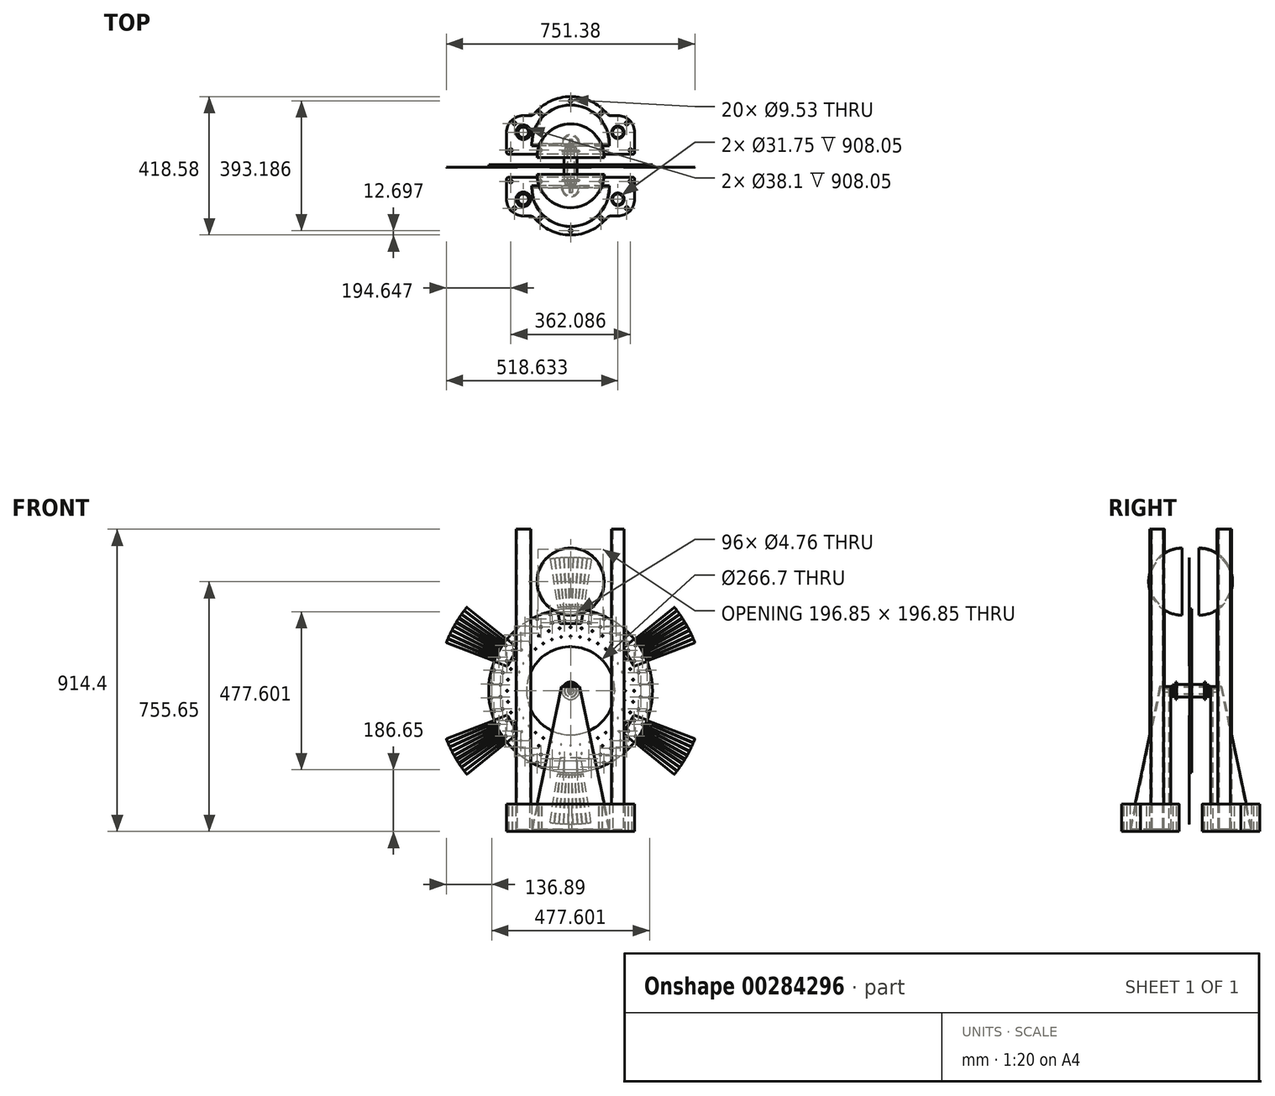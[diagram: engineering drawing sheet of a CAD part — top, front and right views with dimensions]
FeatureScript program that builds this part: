
annotation { "Feature Type Name" : "Feature", "Feature Type Description" : "" }
export const myFeature = defineFeature(function(context is Context, id is Id, definition is map)
    precondition{}
    {
        {
            var Q0;
            Q0=qCreatedBy(makeId("Front.planeOp"),FACE);
            var sketch = newSketch(context, id + "F0", { "sketchPlane" : qUnion([Q0])});
            skLineSegment(sketch, "E0", {"start": v(0, 0) * mm, "end": v(457.2, 0) * mm, "construction": true});
            skCircle(sketch, "E1", {"center": v(0, 0) * mm, "radius": 247.65 * mm});
            skCircle(sketch, "E2", {"center": v(0, 0) * mm, "radius": 133.35 * mm});
            skCircle(sketch, "E3", {"center": v(192.18, 0) * mm, "radius": 2 * mm});
            skCircle(sketch, "E4.1.0", {"center": v(189.26, 33.37) * mm, "radius": 2 * mm});
            skCircle(sketch, "E4.2.0", {"center": v(180.59, 65.73) * mm, "radius": 2 * mm});
            skCircle(sketch, "E4.3.0", {"center": v(166.43, 96.09) * mm, "radius": 2 * mm});
            skCircle(sketch, "E4.4.0", {"center": v(147.22, 123.53) * mm, "radius": 2 * mm});
            skCircle(sketch, "E4.5.0", {"center": v(123.53, 147.22) * mm, "radius": 2 * mm});
            skCircle(sketch, "E4.6.0", {"center": v(96.09, 166.43) * mm, "radius": 2 * mm});
            skCircle(sketch, "E4.7.0", {"center": v(65.73, 180.59) * mm, "radius": 2 * mm});
            skCircle(sketch, "E4.8.0", {"center": v(33.37, 189.26) * mm, "radius": 2 * mm});
            skCircle(sketch, "E4.9.0", {"center": v(0, 192.18) * mm, "radius": 2 * mm});
            skCircle(sketch, "E4.10.0", {"center": v(-33.37, 189.26) * mm, "radius": 2 * mm});
            skCircle(sketch, "E4.11.0", {"center": v(-65.73, 180.59) * mm, "radius": 2 * mm});
            skCircle(sketch, "E4.12.0", {"center": v(-96.09, 166.43) * mm, "radius": 2 * mm});
            skCircle(sketch, "E4.13.0", {"center": v(-123.53, 147.22) * mm, "radius": 2 * mm});
            skCircle(sketch, "E4.14.0", {"center": v(-147.22, 123.53) * mm, "radius": 2 * mm});
            skCircle(sketch, "E4.15.0", {"center": v(-166.43, 96.09) * mm, "radius": 2 * mm});
            skCircle(sketch, "E4.16.0", {"center": v(-180.59, 65.73) * mm, "radius": 2 * mm});
            skCircle(sketch, "E4.17.0", {"center": v(-189.26, 33.37) * mm, "radius": 2 * mm});
            skCircle(sketch, "E4.18.0", {"center": v(-192.18, 0) * mm, "radius": 2 * mm});
            skCircle(sketch, "E4.19.0", {"center": v(-189.26, -33.37) * mm, "radius": 2 * mm});
            skCircle(sketch, "E4.20.0", {"center": v(-180.59, -65.73) * mm, "radius": 2 * mm});
            skCircle(sketch, "E4.21.0", {"center": v(-166.43, -96.09) * mm, "radius": 2 * mm});
            skCircle(sketch, "E4.22.0", {"center": v(-147.22, -123.53) * mm, "radius": 2 * mm});
            skCircle(sketch, "E4.23.0", {"center": v(-123.53, -147.22) * mm, "radius": 2 * mm});
            skCircle(sketch, "E4.24.0", {"center": v(-96.09, -166.43) * mm, "radius": 2 * mm});
            skCircle(sketch, "E4.25.0", {"center": v(-65.73, -180.59) * mm, "radius": 2 * mm});
            skCircle(sketch, "E4.26.0", {"center": v(-33.37, -189.26) * mm, "radius": 2 * mm});
            skCircle(sketch, "E4.27.0", {"center": v(0, -192.18) * mm, "radius": 2 * mm});
            skCircle(sketch, "E4.28.0", {"center": v(33.37, -189.26) * mm, "radius": 2 * mm});
            skCircle(sketch, "E4.29.0", {"center": v(65.73, -180.59) * mm, "radius": 2 * mm});
            skCircle(sketch, "E4.30.0", {"center": v(96.09, -166.43) * mm, "radius": 2 * mm});
            skCircle(sketch, "E4.31.0", {"center": v(123.53, -147.22) * mm, "radius": 2 * mm});
            skCircle(sketch, "E4.32.0", {"center": v(147.22, -123.53) * mm, "radius": 2 * mm});
            skCircle(sketch, "E4.33.0", {"center": v(166.43, -96.09) * mm, "radius": 2 * mm});
            skCircle(sketch, "E4.34.0", {"center": v(180.59, -65.73) * mm, "radius": 2 * mm});
            skCircle(sketch, "E4.35.0", {"center": v(189.26, -33.37) * mm, "radius": 2 * mm});
            skCircle(sketch, "E5", {"center": v(165.1, 0) * mm, "radius": 1.59 * mm});
            skLineSegment(sketch, "E6", {"start": v(0, 0) * mm, "end": v(246.7, 21.58) * mm, "construction": true});
            skCircle(sketch, "E7", {"center": v(238.8, 20.9) * mm, "radius": 2.38 * mm});
            skCircle(sketch, "E8", {"center": v(211.92, 18.54) * mm, "radius": 2.38 * mm});
            skCircle(sketch, "E9.1.0", {"center": v(205.48, 55.06) * mm, "radius": 2.38 * mm});
            skCircle(sketch, "E9.1.1", {"center": v(231.54, 62.04) * mm, "radius": 2.38 * mm});
            skCircle(sketch, "E9.2.0", {"center": v(192.8, 89.9) * mm, "radius": 2.38 * mm});
            skCircle(sketch, "E9.2.1", {"center": v(217.25, 101.3) * mm, "radius": 2.38 * mm});
            skCircle(sketch, "E9.3.0", {"center": v(174.25, 122.01) * mm, "radius": 2.38 * mm});
            skCircle(sketch, "E9.3.1", {"center": v(196.36, 137.5) * mm, "radius": 2.38 * mm});
            skCircle(sketch, "E9.4.0", {"center": v(150.42, 150.42) * mm, "radius": 2.38 * mm});
            skCircle(sketch, "E9.4.1", {"center": v(169.5, 169.5) * mm, "radius": 2.38 * mm});
            skCircle(sketch, "E9.5.0", {"center": v(122.01, 174.25) * mm, "radius": 2.38 * mm});
            skCircle(sketch, "E9.5.1", {"center": v(137.5, 196.36) * mm, "radius": 2.38 * mm});
            skCircle(sketch, "E9.6.0", {"center": v(89.9, 192.8) * mm, "radius": 2.38 * mm});
            skCircle(sketch, "E9.6.1", {"center": v(101.3, 217.25) * mm, "radius": 2.38 * mm});
            skCircle(sketch, "E9.7.0", {"center": v(55.06, 205.48) * mm, "radius": 2.38 * mm});
            skCircle(sketch, "E9.7.1", {"center": v(62.04, 231.54) * mm, "radius": 2.38 * mm});
            skCircle(sketch, "E9.8.0", {"center": v(18.54, 211.92) * mm, "radius": 2.38 * mm});
            skCircle(sketch, "E9.8.1", {"center": v(20.9, 238.8) * mm, "radius": 2.38 * mm});
            skCircle(sketch, "E9.9.0", {"center": v(-18.54, 211.92) * mm, "radius": 2.38 * mm});
            skCircle(sketch, "E9.9.1", {"center": v(-20.9, 238.8) * mm, "radius": 2.38 * mm});
            skCircle(sketch, "E9.10.0", {"center": v(-55.06, 205.48) * mm, "radius": 2.38 * mm});
            skCircle(sketch, "E9.10.1", {"center": v(-62.04, 231.54) * mm, "radius": 2.38 * mm});
            skCircle(sketch, "E9.11.0", {"center": v(-89.9, 192.8) * mm, "radius": 2.38 * mm});
            skCircle(sketch, "E9.11.1", {"center": v(-101.3, 217.25) * mm, "radius": 2.38 * mm});
            skCircle(sketch, "E9.12.0", {"center": v(-122.01, 174.25) * mm, "radius": 2.38 * mm});
            skCircle(sketch, "E9.12.1", {"center": v(-137.5, 196.36) * mm, "radius": 2.38 * mm});
            skCircle(sketch, "E9.13.0", {"center": v(-150.42, 150.42) * mm, "radius": 2.38 * mm});
            skCircle(sketch, "E9.13.1", {"center": v(-169.5, 169.5) * mm, "radius": 2.38 * mm});
            skCircle(sketch, "E9.14.0", {"center": v(-174.25, 122.01) * mm, "radius": 2.38 * mm});
            skCircle(sketch, "E9.14.1", {"center": v(-196.36, 137.5) * mm, "radius": 2.38 * mm});
            skCircle(sketch, "E9.15.0", {"center": v(-192.8, 89.9) * mm, "radius": 2.38 * mm});
            skCircle(sketch, "E9.15.1", {"center": v(-217.25, 101.3) * mm, "radius": 2.38 * mm});
            skCircle(sketch, "E9.16.0", {"center": v(-205.48, 55.06) * mm, "radius": 2.38 * mm});
            skCircle(sketch, "E9.16.1", {"center": v(-231.54, 62.04) * mm, "radius": 2.38 * mm});
            skCircle(sketch, "E9.17.0", {"center": v(-211.92, 18.54) * mm, "radius": 2.38 * mm});
            skCircle(sketch, "E9.17.1", {"center": v(-238.8, 20.9) * mm, "radius": 2.38 * mm});
            skCircle(sketch, "E9.18.0", {"center": v(-211.92, -18.54) * mm, "radius": 2.38 * mm});
            skCircle(sketch, "E9.18.1", {"center": v(-238.8, -20.9) * mm, "radius": 2.38 * mm});
            skCircle(sketch, "E9.19.0", {"center": v(-205.48, -55.06) * mm, "radius": 2.38 * mm});
            skCircle(sketch, "E9.19.1", {"center": v(-231.54, -62.04) * mm, "radius": 2.38 * mm});
            skCircle(sketch, "E9.20.0", {"center": v(-192.8, -89.9) * mm, "radius": 2.38 * mm});
            skCircle(sketch, "E9.20.1", {"center": v(-217.25, -101.3) * mm, "radius": 2.38 * mm});
            skCircle(sketch, "E9.21.0", {"center": v(-174.25, -122.01) * mm, "radius": 2.38 * mm});
            skCircle(sketch, "E9.21.1", {"center": v(-196.36, -137.5) * mm, "radius": 2.38 * mm});
            skCircle(sketch, "E9.22.0", {"center": v(-150.42, -150.42) * mm, "radius": 2.38 * mm});
            skCircle(sketch, "E9.22.1", {"center": v(-169.5, -169.5) * mm, "radius": 2.38 * mm});
            skCircle(sketch, "E9.23.0", {"center": v(-122.01, -174.25) * mm, "radius": 2.38 * mm});
            skCircle(sketch, "E9.23.1", {"center": v(-137.5, -196.36) * mm, "radius": 2.38 * mm});
            skCircle(sketch, "E9.24.0", {"center": v(-89.9, -192.8) * mm, "radius": 2.38 * mm});
            skCircle(sketch, "E9.24.1", {"center": v(-101.3, -217.25) * mm, "radius": 2.38 * mm});
            skCircle(sketch, "E9.25.0", {"center": v(-55.06, -205.48) * mm, "radius": 2.38 * mm});
            skCircle(sketch, "E9.25.1", {"center": v(-62.04, -231.54) * mm, "radius": 2.38 * mm});
            skCircle(sketch, "E9.26.0", {"center": v(-18.54, -211.92) * mm, "radius": 2.38 * mm});
            skCircle(sketch, "E9.26.1", {"center": v(-20.9, -238.8) * mm, "radius": 2.38 * mm});
            skCircle(sketch, "E9.27.0", {"center": v(18.54, -211.92) * mm, "radius": 2.38 * mm});
            skCircle(sketch, "E9.27.1", {"center": v(20.9, -238.8) * mm, "radius": 2.38 * mm});
            skCircle(sketch, "E9.28.0", {"center": v(55.06, -205.48) * mm, "radius": 2.38 * mm});
            skCircle(sketch, "E9.28.1", {"center": v(62.04, -231.54) * mm, "radius": 2.38 * mm});
            skCircle(sketch, "E9.29.0", {"center": v(89.9, -192.8) * mm, "radius": 2.38 * mm});
            skCircle(sketch, "E9.29.1", {"center": v(101.3, -217.25) * mm, "radius": 2.38 * mm});
            skCircle(sketch, "E9.30.0", {"center": v(122.01, -174.25) * mm, "radius": 2.38 * mm});
            skCircle(sketch, "E9.30.1", {"center": v(137.5, -196.36) * mm, "radius": 2.38 * mm});
            skCircle(sketch, "E9.31.0", {"center": v(150.42, -150.42) * mm, "radius": 2.38 * mm});
            skCircle(sketch, "E9.31.1", {"center": v(169.5, -169.5) * mm, "radius": 2.38 * mm});
            skCircle(sketch, "E9.32.0", {"center": v(174.25, -122.01) * mm, "radius": 2.38 * mm});
            skCircle(sketch, "E9.32.1", {"center": v(196.36, -137.5) * mm, "radius": 2.38 * mm});
            skCircle(sketch, "E9.33.0", {"center": v(192.8, -89.9) * mm, "radius": 2.38 * mm});
            skCircle(sketch, "E9.33.1", {"center": v(217.25, -101.3) * mm, "radius": 2.38 * mm});
            skCircle(sketch, "E9.34.0", {"center": v(205.48, -55.06) * mm, "radius": 2.38 * mm});
            skCircle(sketch, "E9.34.1", {"center": v(231.54, -62.04) * mm, "radius": 2.38 * mm});
            skCircle(sketch, "E9.35.0", {"center": v(211.92, -18.54) * mm, "radius": 2.38 * mm});
            skCircle(sketch, "E9.35.1", {"center": v(238.8, -20.9) * mm, "radius": 2.38 * mm});
            skCircle(sketch, "E10.1.0", {"center": v(162.6, 28.67) * mm, "radius": 1.59 * mm});
            skCircle(sketch, "E10.2.0", {"center": v(155.14, 56.47) * mm, "radius": 1.59 * mm});
            skCircle(sketch, "E10.3.0", {"center": v(142.98, 82.55) * mm, "radius": 1.59 * mm});
            skCircle(sketch, "E10.4.0", {"center": v(126.47, 106.12) * mm, "radius": 1.59 * mm});
            skCircle(sketch, "E10.5.0", {"center": v(106.12, 126.47) * mm, "radius": 1.59 * mm});
            skCircle(sketch, "E10.6.0", {"center": v(82.55, 142.98) * mm, "radius": 1.59 * mm});
            skCircle(sketch, "E10.7.0", {"center": v(56.47, 155.14) * mm, "radius": 1.59 * mm});
            skCircle(sketch, "E10.8.0", {"center": v(28.67, 162.6) * mm, "radius": 1.59 * mm});
            skCircle(sketch, "E10.9.0", {"center": v(0, 165.1) * mm, "radius": 1.59 * mm});
            skCircle(sketch, "E10.10.0", {"center": v(-28.67, 162.6) * mm, "radius": 1.59 * mm});
            skCircle(sketch, "E10.11.0", {"center": v(-56.47, 155.14) * mm, "radius": 1.59 * mm});
            skCircle(sketch, "E10.12.0", {"center": v(-82.55, 142.98) * mm, "radius": 1.59 * mm});
            skCircle(sketch, "E10.13.0", {"center": v(-106.12, 126.47) * mm, "radius": 1.59 * mm});
            skCircle(sketch, "E10.14.0", {"center": v(-126.47, 106.12) * mm, "radius": 1.59 * mm});
            skCircle(sketch, "E10.15.0", {"center": v(-142.98, 82.55) * mm, "radius": 1.59 * mm});
            skCircle(sketch, "E10.16.0", {"center": v(-155.14, 56.47) * mm, "radius": 1.59 * mm});
            skCircle(sketch, "E10.17.0", {"center": v(-162.6, 28.67) * mm, "radius": 1.59 * mm});
            skCircle(sketch, "E10.18.0", {"center": v(-165.1, 0) * mm, "radius": 1.59 * mm});
            skCircle(sketch, "E10.19.0", {"center": v(-162.6, -28.67) * mm, "radius": 1.59 * mm});
            skCircle(sketch, "E10.20.0", {"center": v(-155.14, -56.47) * mm, "radius": 1.59 * mm});
            skCircle(sketch, "E10.21.0", {"center": v(-142.98, -82.55) * mm, "radius": 1.59 * mm});
            skCircle(sketch, "E10.22.0", {"center": v(-126.47, -106.12) * mm, "radius": 1.59 * mm});
            skCircle(sketch, "E10.23.0", {"center": v(-106.12, -126.47) * mm, "radius": 1.59 * mm});
            skCircle(sketch, "E10.24.0", {"center": v(-82.55, -142.98) * mm, "radius": 1.59 * mm});
            skCircle(sketch, "E10.25.0", {"center": v(-56.47, -155.14) * mm, "radius": 1.59 * mm});
            skCircle(sketch, "E10.26.0", {"center": v(-28.67, -162.6) * mm, "radius": 1.59 * mm});
            skCircle(sketch, "E10.27.0", {"center": v(0, -165.1) * mm, "radius": 1.59 * mm});
            skCircle(sketch, "E10.28.0", {"center": v(28.67, -162.6) * mm, "radius": 1.59 * mm});
            skCircle(sketch, "E10.29.0", {"center": v(56.47, -155.14) * mm, "radius": 1.59 * mm});
            skCircle(sketch, "E10.30.0", {"center": v(82.55, -142.98) * mm, "radius": 1.59 * mm});
            skCircle(sketch, "E10.31.0", {"center": v(106.12, -126.47) * mm, "radius": 1.59 * mm});
            skCircle(sketch, "E10.32.0", {"center": v(126.47, -106.12) * mm, "radius": 1.59 * mm});
            skCircle(sketch, "E10.33.0", {"center": v(142.98, -82.55) * mm, "radius": 1.59 * mm});
            skCircle(sketch, "E10.34.0", {"center": v(155.14, -56.47) * mm, "radius": 1.59 * mm});
            skCircle(sketch, "E10.35.0", {"center": v(162.6, -28.67) * mm, "radius": 1.59 * mm});
            skLineSegment(sketch, "E11", {"start": v(165.1, 0) * mm, "end": v(192.18, 0) * mm, "construction": true});
            skLineSegment(sketch, "E12", {"start": v(192.18, 0) * mm, "end": v(211.92, 18.54) * mm, "construction": true});
            skSolve(sketch);
        }
        {
            var Q0;
            Q0=makeQuery(id+"F0.imprint","IMPRINT",FACE,{"disambiguationData":[TD([[makeQuery(id+"F0.imprint","IMPRINT",EDGE,{"derivedFrom":sQuery(id+"F0.wireOp",EDGE,"E1")}),1.0]])]});
            extrude(context, id + "F1", {"entities" : qUnion([Q0]), "endBound" : BoundingType.SYMMETRIC, "depth" : 6.35 * mm});
        }
        {
            var Q0;
            Q0=makeQuery(id+"F1.opExtrude","CAP_FACE",FACE,{"disambiguationData":[OSD([sQuery(id+"F0.wireOp",EDGE,"E1"),sQuery(id+"F0.wireOp",EDGE,"E2"),sQuery(id+"F0.wireOp",EDGE,"E3"),sQuery(id+"F0.wireOp",EDGE,"E4.1.0"),sQuery(id+"F0.wireOp",EDGE,"E4.2.0"),sQuery(id+"F0.wireOp",EDGE,"E4.3.0"),sQuery(id+"F0.wireOp",EDGE,"E4.4.0"),sQuery(id+"F0.wireOp",EDGE,"E4.5.0"),sQuery(id+"F0.wireOp",EDGE,"E4.6.0"),sQuery(id+"F0.wireOp",EDGE,"E4.7.0"),sQuery(id+"F0.wireOp",EDGE,"E4.8.0"),sQuery(id+"F0.wireOp",EDGE,"E4.9.0"),sQuery(id+"F0.wireOp",EDGE,"E4.10.0"),sQuery(id+"F0.wireOp",EDGE,"E4.11.0"),sQuery(id+"F0.wireOp",EDGE,"E4.12.0"),sQuery(id+"F0.wireOp",EDGE,"E4.13.0"),sQuery(id+"F0.wireOp",EDGE,"E4.14.0"),sQuery(id+"F0.wireOp",EDGE,"E4.15.0"),sQuery(id+"F0.wireOp",EDGE,"E4.16.0"),sQuery(id+"F0.wireOp",EDGE,"E4.17.0"),sQuery(id+"F0.wireOp",EDGE,"E4.18.0"),sQuery(id+"F0.wireOp",EDGE,"E4.19.0"),sQuery(id+"F0.wireOp",EDGE,"E4.20.0"),sQuery(id+"F0.wireOp",EDGE,"E4.21.0"),sQuery(id+"F0.wireOp",EDGE,"E4.22.0"),sQuery(id+"F0.wireOp",EDGE,"E4.23.0"),sQuery(id+"F0.wireOp",EDGE,"E4.24.0"),sQuery(id+"F0.wireOp",EDGE,"E4.25.0"),sQuery(id+"F0.wireOp",EDGE,"E4.26.0"),sQuery(id+"F0.wireOp",EDGE,"E4.27.0"),sQuery(id+"F0.wireOp",EDGE,"E4.28.0"),sQuery(id+"F0.wireOp",EDGE,"E4.29.0"),sQuery(id+"F0.wireOp",EDGE,"E4.30.0"),sQuery(id+"F0.wireOp",EDGE,"E4.31.0"),sQuery(id+"F0.wireOp",EDGE,"E4.32.0"),sQuery(id+"F0.wireOp",EDGE,"E4.33.0"),sQuery(id+"F0.wireOp",EDGE,"E4.34.0"),sQuery(id+"F0.wireOp",EDGE,"E4.35.0"),sQuery(id+"F0.wireOp",EDGE,"E5"),sQuery(id+"F0.wireOp",EDGE,"E7"),sQuery(id+"F0.wireOp",EDGE,"E8"),sQuery(id+"F0.wireOp",EDGE,"E9.1.0"),sQuery(id+"F0.wireOp",EDGE,"E9.1.1"),sQuery(id+"F0.wireOp",EDGE,"E9.2.0"),sQuery(id+"F0.wireOp",EDGE,"E9.2.1"),sQuery(id+"F0.wireOp",EDGE,"E9.3.0"),sQuery(id+"F0.wireOp",EDGE,"E9.3.1"),sQuery(id+"F0.wireOp",EDGE,"E9.4.0"),sQuery(id+"F0.wireOp",EDGE,"E9.4.1"),sQuery(id+"F0.wireOp",EDGE,"E9.5.0"),sQuery(id+"F0.wireOp",EDGE,"E9.5.1"),sQuery(id+"F0.wireOp",EDGE,"E9.6.0"),sQuery(id+"F0.wireOp",EDGE,"E9.6.1"),sQuery(id+"F0.wireOp",EDGE,"E9.7.0"),sQuery(id+"F0.wireOp",EDGE,"E9.7.1"),sQuery(id+"F0.wireOp",EDGE,"E9.8.0"),sQuery(id+"F0.wireOp",EDGE,"E9.8.1"),sQuery(id+"F0.wireOp",EDGE,"E9.9.0"),sQuery(id+"F0.wireOp",EDGE,"E9.9.1"),sQuery(id+"F0.wireOp",EDGE,"E9.10.0"),sQuery(id+"F0.wireOp",EDGE,"E9.10.1"),sQuery(id+"F0.wireOp",EDGE,"E9.11.0"),sQuery(id+"F0.wireOp",EDGE,"E9.11.1"),sQuery(id+"F0.wireOp",EDGE,"E9.12.0"),sQuery(id+"F0.wireOp",EDGE,"E9.12.1"),sQuery(id+"F0.wireOp",EDGE,"E9.13.0"),sQuery(id+"F0.wireOp",EDGE,"E9.13.1"),sQuery(id+"F0.wireOp",EDGE,"E9.14.0"),sQuery(id+"F0.wireOp",EDGE,"E9.14.1"),sQuery(id+"F0.wireOp",EDGE,"E9.15.0"),sQuery(id+"F0.wireOp",EDGE,"E9.15.1"),sQuery(id+"F0.wireOp",EDGE,"E9.16.0"),sQuery(id+"F0.wireOp",EDGE,"E9.16.1"),sQuery(id+"F0.wireOp",EDGE,"E9.17.0"),sQuery(id+"F0.wireOp",EDGE,"E9.17.1"),sQuery(id+"F0.wireOp",EDGE,"E9.18.0"),sQuery(id+"F0.wireOp",EDGE,"E9.18.1"),sQuery(id+"F0.wireOp",EDGE,"E9.19.0"),sQuery(id+"F0.wireOp",EDGE,"E9.19.1"),sQuery(id+"F0.wireOp",EDGE,"E9.20.0"),sQuery(id+"F0.wireOp",EDGE,"E9.20.1"),sQuery(id+"F0.wireOp",EDGE,"E9.21.0"),sQuery(id+"F0.wireOp",EDGE,"E9.21.1"),sQuery(id+"F0.wireOp",EDGE,"E9.22.0"),sQuery(id+"F0.wireOp",EDGE,"E9.22.1"),sQuery(id+"F0.wireOp",EDGE,"E9.23.0"),sQuery(id+"F0.wireOp",EDGE,"E9.23.1"),sQuery(id+"F0.wireOp",EDGE,"E9.24.0"),sQuery(id+"F0.wireOp",EDGE,"E9.24.1"),sQuery(id+"F0.wireOp",EDGE,"E9.25.0"),sQuery(id+"F0.wireOp",EDGE,"E9.25.1"),sQuery(id+"F0.wireOp",EDGE,"E9.26.0"),sQuery(id+"F0.wireOp",EDGE,"E9.26.1"),sQuery(id+"F0.wireOp",EDGE,"E9.27.0"),sQuery(id+"F0.wireOp",EDGE,"E9.27.1"),sQuery(id+"F0.wireOp",EDGE,"E9.28.0"),sQuery(id+"F0.wireOp",EDGE,"E9.28.1"),sQuery(id+"F0.wireOp",EDGE,"E9.29.0"),sQuery(id+"F0.wireOp",EDGE,"E9.29.1"),sQuery(id+"F0.wireOp",EDGE,"E9.30.0"),sQuery(id+"F0.wireOp",EDGE,"E9.30.1"),sQuery(id+"F0.wireOp",EDGE,"E9.31.0"),sQuery(id+"F0.wireOp",EDGE,"E9.31.1"),sQuery(id+"F0.wireOp",EDGE,"E9.32.0"),sQuery(id+"F0.wireOp",EDGE,"E9.32.1"),sQuery(id+"F0.wireOp",EDGE,"E9.33.0"),sQuery(id+"F0.wireOp",EDGE,"E9.33.1"),sQuery(id+"F0.wireOp",EDGE,"E9.34.0"),sQuery(id+"F0.wireOp",EDGE,"E9.34.1"),sQuery(id+"F0.wireOp",EDGE,"E9.35.0"),sQuery(id+"F0.wireOp",EDGE,"E9.35.1"),sQuery(id+"F0.wireOp",EDGE,"E10.1.0"),sQuery(id+"F0.wireOp",EDGE,"E10.2.0"),sQuery(id+"F0.wireOp",EDGE,"E10.3.0"),sQuery(id+"F0.wireOp",EDGE,"E10.4.0"),sQuery(id+"F0.wireOp",EDGE,"E10.5.0"),sQuery(id+"F0.wireOp",EDGE,"E10.6.0"),sQuery(id+"F0.wireOp",EDGE,"E10.7.0"),sQuery(id+"F0.wireOp",EDGE,"E10.8.0"),sQuery(id+"F0.wireOp",EDGE,"E10.9.0"),sQuery(id+"F0.wireOp",EDGE,"E10.10.0"),sQuery(id+"F0.wireOp",EDGE,"E10.11.0"),sQuery(id+"F0.wireOp",EDGE,"E10.12.0"),sQuery(id+"F0.wireOp",EDGE,"E10.13.0"),sQuery(id+"F0.wireOp",EDGE,"E10.14.0"),sQuery(id+"F0.wireOp",EDGE,"E10.15.0"),sQuery(id+"F0.wireOp",EDGE,"E10.16.0"),sQuery(id+"F0.wireOp",EDGE,"E10.17.0"),sQuery(id+"F0.wireOp",EDGE,"E10.18.0"),sQuery(id+"F0.wireOp",EDGE,"E10.19.0"),sQuery(id+"F0.wireOp",EDGE,"E10.20.0"),sQuery(id+"F0.wireOp",EDGE,"E10.21.0"),sQuery(id+"F0.wireOp",EDGE,"E10.22.0"),sQuery(id+"F0.wireOp",EDGE,"E10.23.0"),sQuery(id+"F0.wireOp",EDGE,"E10.24.0"),sQuery(id+"F0.wireOp",EDGE,"E10.25.0"),sQuery(id+"F0.wireOp",EDGE,"E10.26.0"),sQuery(id+"F0.wireOp",EDGE,"E10.27.0"),sQuery(id+"F0.wireOp",EDGE,"E10.28.0"),sQuery(id+"F0.wireOp",EDGE,"E10.29.0"),sQuery(id+"F0.wireOp",EDGE,"E10.30.0"),sQuery(id+"F0.wireOp",EDGE,"E10.31.0"),sQuery(id+"F0.wireOp",EDGE,"E10.32.0"),sQuery(id+"F0.wireOp",EDGE,"E10.33.0"),sQuery(id+"F0.wireOp",EDGE,"E10.34.0"),sQuery(id+"F0.wireOp",EDGE,"E10.35.0")])],"isStart":false});
            var sketch = newSketch(context, id + "F2", { "sketchPlane" : qUnion([Q0])});
            skLineSegment(sketch, "E13", {"start": v(-63.33, 399.83) * mm, "end": v(0, 0) * mm, "construction": true});
            skLineSegment(sketch, "E14", {"start": v(0, 0) * mm, "end": v(63.33, 399.83) * mm, "construction": true});
            skLineSegment(sketch, "E15", {"start": v(0, 0) * mm, "end": v(0, 404.81) * mm, "construction": true});
            skLineSegment(sketch, "E16", {"start": v(-63.33, 399.83) * mm, "end": v(-63.33, 399.83) * mm});
            skLineSegment(sketch, "E17", {"start": v(-62.83, 396.68) * mm, "end": v(-32.6, 205.88) * mm});
            skLineSegment(sketch, "E18", {"start": v(-29.47, 203.2) * mm, "end": v(29.47, 203.2) * mm});
            skLineSegment(sketch, "E19", {"start": v(32.6, 205.88) * mm, "end": v(62.83, 396.68) * mm});
            skPoint(sketch, "E20.visualSharp", {"position": v(-32.18, 203.2) * mm});
            skArc(sketch, "E20.filletArc", {"start": v(-32.6, 205.88) * mm, "mid": v(-31.53, 203.96) * mm, "end": v(-29.47, 203.2) * mm});
            skPoint(sketch, "E21.visualSharp", {"position": v(32.18, 203.2) * mm});
            skArc(sketch, "E21.filletArc", {"start": v(29.47, 203.2) * mm, "mid": v(31.53, 203.96) * mm, "end": v(32.6, 205.88) * mm});
            skArc(sketch, "E22", {"start": v(-60.16, 400.32) * mm, "mid": v(0, 404.81) * mm, "end": v(60.16, 400.32) * mm});
            skLineSegment(sketch, "E23", {"start": v(63.33, 399.83) * mm, "end": v(63.33, 399.83) * mm});
            skCircle(sketch, "E24.0", {"center": v(-20.9, 238.8) * mm, "radius": 2.38 * mm});
            skCircle(sketch, "E25.0", {"center": v(20.9, 238.8) * mm, "radius": 2.38 * mm});
            skCircle(sketch, "E26.0", {"center": v(18.54, 211.92) * mm, "radius": 2.38 * mm});
            skCircle(sketch, "E27.0", {"center": v(-18.54, 211.92) * mm, "radius": 2.38 * mm});
            skPoint(sketch, "E28.visualSharp", {"position": v(-63.33, 399.83) * mm});
            skArc(sketch, "E28.filletArc", {"start": v(-60.16, 400.32) * mm, "mid": v(-62.25, 399.05) * mm, "end": v(-62.83, 396.68) * mm});
            skPoint(sketch, "E29.visualSharp", {"position": v(63.33, 399.83) * mm});
            skArc(sketch, "E29.filletArc", {"start": v(62.83, 396.68) * mm, "mid": v(62.25, 399.05) * mm, "end": v(60.16, 400.32) * mm});
            skSolve(sketch);
        }
        {
            var Q0;
            Q0=makeQuery(id+"F2.imprint","IMPRINT",FACE,{"disambiguationData":[TD([[makeQuery(id+"F2.imprint","IMPRINT",EDGE,{"derivedFrom":sQuery(id+"F2.wireOp",EDGE,"E22")}),-1.0]])]});
            var Q1;
            Q1=makeQuery(id+"F2.imprint","IMPRINT",FACE,{"disambiguationData":[TD([[makeQuery(id+"F2.imprint","IMPRINT",EDGE,{"derivedFrom":sQuery(id+"F2.wireOp",EDGE,"E18")}),1.0]])]});
            extrude(context, id + "F3", {"entities" : qUnion([Q0, Q1]), "depth" : 1.59 * mm});
        }
        {
            var Q0;
            Q0=makeQuery(id+"F3.opExtrude","CAP_FACE",FACE,{"disambiguationData":[OSD([sQuery(id+"F2.wireOp",EDGE,"E17"),sQuery(id+"F2.wireOp",EDGE,"E18"),sQuery(id+"F2.wireOp",EDGE,"E19"),sQuery(id+"F2.wireOp",EDGE,"E20.filletArc"),sQuery(id+"F2.wireOp",EDGE,"E21.filletArc"),sQuery(id+"F2.wireOp",EDGE,"E22"),sQuery(id+"F2.wireOp",EDGE,"E24.0"),sQuery(id+"F2.wireOp",EDGE,"E25.0"),sQuery(id+"F2.wireOp",EDGE,"E26.0"),sQuery(id+"F2.wireOp",EDGE,"E27.0"),sQuery(id+"F2.wireOp",EDGE,"E28.filletArc"),sQuery(id+"F2.wireOp",EDGE,"E29.filletArc")])],"isStart":false});
            var sketch = newSketch(context, id + "F4", { "sketchPlane" : qUnion([Q0])});
            skLineSegment(sketch, "E30", {"start": v(0, 0) * mm, "end": v(0, 404.81) * mm, "construction": true});
            skLineSegment(sketch, "E31", {"start": v(0, 0) * mm, "end": v(-7.06, 404.75) * mm, "construction": true});
            skLineSegment(sketch, "E32", {"start": v(0, 0) * mm, "end": v(7.06, 404.75) * mm, "construction": true});
            skLineSegment(sketch, "E33", {"start": v(-6.22, 401.58) * mm, "end": v(-3.67, 255.55) * mm});
            skLineSegment(sketch, "E34", {"start": v(6.22, 401.58) * mm, "end": v(3.67, 255.55) * mm});
            skArc(sketch, "E35", {"start": v(-4.65, 403.2) * mm, "mid": v(0, 403.23) * mm, "end": v(4.65, 403.2) * mm});
            skArc(sketch, "E36", {"start": v(-2.07, 254) * mm, "mid": v(0, 254) * mm, "end": v(2.07, 254) * mm});
            skPoint(sketch, "E37.visualSharp", {"position": v(-6.24, 403.18) * mm});
            skArc(sketch, "E37.filletArc", {"start": v(-4.65, 403.2) * mm, "mid": v(-5.77, 402.72) * mm, "end": v(-6.22, 401.58) * mm});
            skPoint(sketch, "E38.visualSharp", {"position": v(6.24, 403.18) * mm});
            skArc(sketch, "E38.filletArc", {"start": v(6.22, 401.58) * mm, "mid": v(5.77, 402.72) * mm, "end": v(4.65, 403.2) * mm});
            skArc(sketch, "E39.filletArc", {"start": v(-3.67, 255.55) * mm, "mid": v(-3.19, 254.44) * mm, "end": v(-2.07, 254) * mm});
            skPoint(sketch, "E40.visualSharp", {"position": v(3.64, 253.97) * mm});
            skArc(sketch, "E40.filletArc", {"start": v(2.07, 254) * mm, "mid": v(3.19, 254.44) * mm, "end": v(3.67, 255.55) * mm});
            skPoint(sketch, "E41.1.0", {"position": v(7.83, 403.15) * mm});
            skPoint(sketch, "E41.1.1", {"position": v(12.5, 253.7) * mm});
            skPoint(sketch, "E41.1.2", {"position": v(20.31, 402.71) * mm});
            skLineSegment(sketch, "E41.1.3", {"start": v(7.8, 401.56) * mm, "end": v(5.25, 255.52) * mm});
            skLineSegment(sketch, "E41.1.4", {"start": v(20.23, 401.12) * mm, "end": v(12.58, 255.27) * mm});
            skArc(sketch, "E41.1.5", {"start": v(9.43, 403.11) * mm, "mid": v(14.07, 402.98) * mm, "end": v(18.72, 402.8) * mm});
            skArc(sketch, "E41.1.6", {"start": v(6.8, 253.9) * mm, "mid": v(8.86, 253.85) * mm, "end": v(10.93, 253.76) * mm});
            skArc(sketch, "E41.1.7", {"start": v(10.93, 253.76) * mm, "mid": v(12.07, 254.18) * mm, "end": v(12.58, 255.27) * mm});
            skArc(sketch, "E41.1.8", {"start": v(5.25, 255.52) * mm, "mid": v(5.7, 254.4) * mm, "end": v(6.8, 253.9) * mm});
            skArc(sketch, "E41.1.9", {"start": v(20.23, 401.12) * mm, "mid": v(19.82, 402.27) * mm, "end": v(18.72, 402.8) * mm});
            skArc(sketch, "E41.1.10", {"start": v(9.43, 403.11) * mm, "mid": v(8.3, 402.67) * mm, "end": v(7.8, 401.56) * mm});
            skPoint(sketch, "E41.2.0", {"position": v(21.9, 402.63) * mm});
            skPoint(sketch, "E41.2.1", {"position": v(21.35, 253.1) * mm});
            skPoint(sketch, "E41.2.2", {"position": v(34.35, 401.76) * mm});
            skLineSegment(sketch, "E41.2.3", {"start": v(21.81, 401.04) * mm, "end": v(14.17, 255.18) * mm});
            skLineSegment(sketch, "E41.2.4", {"start": v(34.21, 400.17) * mm, "end": v(21.48, 254.67) * mm});
            skArc(sketch, "E41.2.5", {"start": v(23.5, 402.54) * mm, "mid": v(28.13, 402.24) * mm, "end": v(32.76, 401.9) * mm});
            skArc(sketch, "E41.2.6", {"start": v(15.66, 253.52) * mm, "mid": v(17.72, 253.38) * mm, "end": v(19.78, 253.23) * mm});
            skArc(sketch, "E41.2.7", {"start": v(19.78, 253.23) * mm, "mid": v(20.93, 253.6) * mm, "end": v(21.48, 254.67) * mm});
            skArc(sketch, "E41.2.8", {"start": v(14.17, 255.18) * mm, "mid": v(14.57, 254.04) * mm, "end": v(15.66, 253.52) * mm});
            skArc(sketch, "E41.2.9", {"start": v(34.21, 400.17) * mm, "mid": v(33.85, 401.33) * mm, "end": v(32.76, 401.9) * mm});
            skArc(sketch, "E41.2.10", {"start": v(23.5, 402.54) * mm, "mid": v(22.34, 402.14) * mm, "end": v(21.81, 401.04) * mm});
            skPoint(sketch, "E41.3.0", {"position": v(35.93, 401.62) * mm});
            skPoint(sketch, "E41.3.1", {"position": v(30.17, 252.2) * mm});
            skPoint(sketch, "E41.3.2", {"position": v(48.35, 400.32) * mm});
            skLineSegment(sketch, "E41.3.3", {"start": v(35.8, 400.03) * mm, "end": v(23.07, 254.53) * mm});
            skLineSegment(sketch, "E41.3.4", {"start": v(48.16, 398.73) * mm, "end": v(30.36, 253.77) * mm});
            skArc(sketch, "E41.3.5", {"start": v(37.52, 401.48) * mm, "mid": v(42.15, 401.02) * mm, "end": v(46.77, 400.5) * mm});
            skArc(sketch, "E41.3.6", {"start": v(24.5, 252.82) * mm, "mid": v(26.55, 252.6) * mm, "end": v(28.6, 252.38) * mm});
            skArc(sketch, "E41.3.7", {"start": v(28.6, 252.38) * mm, "mid": v(29.77, 252.72) * mm, "end": v(30.36, 253.77) * mm});
            skArc(sketch, "E41.3.8", {"start": v(23.07, 254.53) * mm, "mid": v(23.43, 253.38) * mm, "end": v(24.5, 252.82) * mm});
            skArc(sketch, "E41.3.9", {"start": v(48.16, 398.73) * mm, "mid": v(47.83, 399.9) * mm, "end": v(46.77, 400.5) * mm});
            skArc(sketch, "E41.3.10", {"start": v(37.52, 401.48) * mm, "mid": v(36.36, 401.11) * mm, "end": v(35.8, 400.03) * mm});
            skPoint(sketch, "E41.4.0", {"position": v(49.93, 400.12) * mm});
            skPoint(sketch, "E41.4.1", {"position": v(38.95, 251) * mm});
            skPoint(sketch, "E41.4.2", {"position": v(62.3, 398.38) * mm});
            skLineSegment(sketch, "E41.4.3", {"start": v(49.73, 398.54) * mm, "end": v(31.93, 253.57) * mm});
            skLineSegment(sketch, "E41.4.4", {"start": v(62.04, 396.8) * mm, "end": v(39.2, 252.55) * mm});
            skArc(sketch, "E41.4.5", {"start": v(51.51, 399.92) * mm, "mid": v(56.12, 399.3) * mm, "end": v(60.72, 398.63) * mm});
            skArc(sketch, "E41.4.6", {"start": v(33.3, 251.8) * mm, "mid": v(35.35, 251.53) * mm, "end": v(37.4, 251.23) * mm});
            skArc(sketch, "E41.4.7", {"start": v(37.4, 251.23) * mm, "mid": v(38.57, 251.52) * mm, "end": v(39.2, 252.55) * mm});
            skArc(sketch, "E41.4.8", {"start": v(31.93, 253.57) * mm, "mid": v(32.25, 252.4) * mm, "end": v(33.3, 251.8) * mm});
            skArc(sketch, "E41.4.9", {"start": v(62.04, 396.8) * mm, "mid": v(61.76, 398) * mm, "end": v(60.72, 398.63) * mm});
            skArc(sketch, "E41.4.10", {"start": v(51.51, 399.92) * mm, "mid": v(50.34, 399.6) * mm, "end": v(49.73, 398.54) * mm});
            skLineSegment(sketch, "E41.anchor1", {"start": v(0, 0) * mm, "end": v(-3.67, 255.55) * mm, "construction": true});
            skLineSegment(sketch, "E41.anchor2", {"start": v(0, 0) * mm, "end": v(31.93, 253.57) * mm, "construction": true});
            skPoint(sketch, "E42.1.0", {"position": v(-7.78, 403.15) * mm});
            skLineSegment(sketch, "E42.1.1", {"start": v(-20.17, 401.12) * mm, "end": v(-12.53, 255.27) * mm});
            skLineSegment(sketch, "E42.1.2", {"start": v(-7.75, 401.56) * mm, "end": v(-5.2, 255.53) * mm});
            skArc(sketch, "E42.1.3", {"start": v(-18.66, 402.8) * mm, "mid": v(-14.02, 402.98) * mm, "end": v(-9.37, 403.12) * mm});
            skPoint(sketch, "E42.1.4", {"position": v(-5.17, 253.95) * mm});
            skPoint(sketch, "E42.1.5", {"position": v(-20.26, 402.72) * mm});
            skArc(sketch, "E42.1.6", {"start": v(-10.87, 253.77) * mm, "mid": v(-8.8, 253.85) * mm, "end": v(-6.74, 253.91) * mm});
            skArc(sketch, "E42.1.7", {"start": v(-18.66, 402.8) * mm, "mid": v(-19.76, 402.27) * mm, "end": v(-20.17, 401.12) * mm});
            skArc(sketch, "E42.1.8", {"start": v(-7.75, 401.56) * mm, "mid": v(-8.24, 402.67) * mm, "end": v(-9.37, 403.12) * mm});
            skArc(sketch, "E42.1.9", {"start": v(-12.53, 255.27) * mm, "mid": v(-12.01, 254.18) * mm, "end": v(-10.87, 253.77) * mm});
            skArc(sketch, "E42.1.10", {"start": v(-6.74, 253.91) * mm, "mid": v(-5.64, 254.4) * mm, "end": v(-5.2, 255.53) * mm});
            skPoint(sketch, "E42.2.0", {"position": v(-21.79, 402.64) * mm});
            skLineSegment(sketch, "E42.2.1", {"start": v(-34.1, 400.18) * mm, "end": v(-21.37, 254.68) * mm});
            skLineSegment(sketch, "E42.2.2", {"start": v(-21.7, 401.04) * mm, "end": v(-14.06, 255.2) * mm});
            skArc(sketch, "E42.2.3", {"start": v(-32.65, 401.9) * mm, "mid": v(-28.02, 402.25) * mm, "end": v(-23.38, 402.55) * mm});
            skPoint(sketch, "E42.2.4", {"position": v(-13.98, 253.61) * mm});
            skPoint(sketch, "E42.2.5", {"position": v(-34.24, 401.76) * mm});
            skArc(sketch, "E42.2.6", {"start": v(-19.67, 253.23) * mm, "mid": v(-17.6, 253.39) * mm, "end": v(-15.55, 253.52) * mm});
            skArc(sketch, "E42.2.7", {"start": v(-32.65, 401.9) * mm, "mid": v(-33.73, 401.34) * mm, "end": v(-34.1, 400.18) * mm});
            skArc(sketch, "E42.2.8", {"start": v(-21.7, 401.04) * mm, "mid": v(-22.23, 402.14) * mm, "end": v(-23.38, 402.55) * mm});
            skArc(sketch, "E42.2.9", {"start": v(-21.37, 254.68) * mm, "mid": v(-20.82, 253.6) * mm, "end": v(-19.67, 253.23) * mm});
            skArc(sketch, "E42.2.10", {"start": v(-15.55, 253.52) * mm, "mid": v(-14.46, 254.05) * mm, "end": v(-14.06, 255.2) * mm});
            skPoint(sketch, "E42.3.0", {"position": v(-35.77, 401.63) * mm});
            skLineSegment(sketch, "E42.3.1", {"start": v(-48, 398.75) * mm, "end": v(-30.2, 253.78) * mm});
            skLineSegment(sketch, "E42.3.2", {"start": v(-35.63, 400.04) * mm, "end": v(-22.9, 254.55) * mm});
            skArc(sketch, "E42.3.3", {"start": v(-46.6, 400.52) * mm, "mid": v(-41.98, 401.03) * mm, "end": v(-37.36, 401.49) * mm});
            skPoint(sketch, "E42.3.4", {"position": v(-22.76, 252.97) * mm});
            skPoint(sketch, "E42.3.5", {"position": v(-48.19, 400.33) * mm});
            skArc(sketch, "E42.3.6", {"start": v(-28.44, 252.4) * mm, "mid": v(-26.38, 252.62) * mm, "end": v(-24.33, 252.83) * mm});
            skArc(sketch, "E42.3.7", {"start": v(-46.6, 400.52) * mm, "mid": v(-47.67, 399.92) * mm, "end": v(-48, 398.75) * mm});
            skArc(sketch, "E42.3.8", {"start": v(-35.63, 400.04) * mm, "mid": v(-36.2, 401.13) * mm, "end": v(-37.36, 401.49) * mm});
            skArc(sketch, "E42.3.9", {"start": v(-30.2, 253.78) * mm, "mid": v(-29.6, 252.73) * mm, "end": v(-28.44, 252.4) * mm});
            skArc(sketch, "E42.3.10", {"start": v(-24.33, 252.83) * mm, "mid": v(-23.26, 253.4) * mm, "end": v(-22.9, 254.55) * mm});
            skPoint(sketch, "E42.4.0", {"position": v(-49.7, 400.14) * mm});
            skLineSegment(sketch, "E42.4.1", {"start": v(-61.82, 396.83) * mm, "end": v(-38.98, 252.57) * mm});
            skLineSegment(sketch, "E42.4.2", {"start": v(-49.51, 398.56) * mm, "end": v(-31.71, 253.6) * mm});
            skArc(sketch, "E42.4.3", {"start": v(-60.5, 398.65) * mm, "mid": v(-55.9, 399.32) * mm, "end": v(-51.3, 399.94) * mm});
            skPoint(sketch, "E42.4.4", {"position": v(-31.52, 252.03) * mm});
            skPoint(sketch, "E42.4.5", {"position": v(-62.07, 398.4) * mm});
            skArc(sketch, "E42.4.6", {"start": v(-37.17, 251.25) * mm, "mid": v(-35.13, 251.55) * mm, "end": v(-33.08, 251.83) * mm});
            skArc(sketch, "E42.4.7", {"start": v(-60.5, 398.65) * mm, "mid": v(-61.54, 398.01) * mm, "end": v(-61.82, 396.83) * mm});
            skArc(sketch, "E42.4.8", {"start": v(-49.51, 398.56) * mm, "mid": v(-50.12, 399.62) * mm, "end": v(-51.3, 399.94) * mm});
            skArc(sketch, "E42.4.9", {"start": v(-38.98, 252.57) * mm, "mid": v(-38.35, 251.54) * mm, "end": v(-37.17, 251.25) * mm});
            skArc(sketch, "E42.4.10", {"start": v(-33.08, 251.83) * mm, "mid": v(-32.03, 252.43) * mm, "end": v(-31.71, 253.6) * mm});
            skPoint(sketch, "E42.center", {"position": v(-0.03, 1.59) * mm});
            skLineSegment(sketch, "E42.anchor1", {"start": v(-0.03, 1.59) * mm, "end": v(-3.67, 255.55) * mm, "construction": true});
            skLineSegment(sketch, "E42.anchor2", {"start": v(-0.03, 1.59) * mm, "end": v(-38.98, 252.57) * mm, "construction": true});
            skSolve(sketch);
        }
        {
            var Q0;
            Q0=makeQuery(id+"F4.imprint","IMPRINT",FACE,{"disambiguationData":[TD([[makeQuery(id+"F4.imprint","IMPRINT",EDGE,{"derivedFrom":sQuery(id+"F4.wireOp",EDGE,"E42.4.1")}),1.0]])]});
            var Q1;
            Q1=makeQuery(id+"F4.imprint","IMPRINT",FACE,{"disambiguationData":[TD([[makeQuery(id+"F4.imprint","IMPRINT",EDGE,{"derivedFrom":sQuery(id+"F4.wireOp",EDGE,"E42.3.1")}),1.0]])]});
            var Q2;
            Q2=makeQuery(id+"F4.imprint","IMPRINT",FACE,{"disambiguationData":[TD([[makeQuery(id+"F4.imprint","IMPRINT",EDGE,{"derivedFrom":sQuery(id+"F4.wireOp",EDGE,"E42.2.1")}),1.0]])]});
            var Q3;
            Q3=makeQuery(id+"F4.imprint","IMPRINT",FACE,{"disambiguationData":[TD([[makeQuery(id+"F4.imprint","IMPRINT",EDGE,{"derivedFrom":sQuery(id+"F4.wireOp",EDGE,"E42.1.1")}),1.0]])]});
            var Q4;
            Q4=makeQuery(id+"F4.imprint","IMPRINT",FACE,{"disambiguationData":[TD([[makeQuery(id+"F4.imprint","IMPRINT",EDGE,{"derivedFrom":sQuery(id+"F4.wireOp",EDGE,"E33")}),1.0]])]});
            var Q5;
            Q5=makeQuery(id+"F4.imprint","IMPRINT",FACE,{"disambiguationData":[TD([[makeQuery(id+"F4.imprint","IMPRINT",EDGE,{"derivedFrom":sQuery(id+"F4.wireOp",EDGE,"E41.1.3")}),1.0]])]});
            var Q6;
            Q6=makeQuery(id+"F4.imprint","IMPRINT",FACE,{"disambiguationData":[TD([[makeQuery(id+"F4.imprint","IMPRINT",EDGE,{"derivedFrom":sQuery(id+"F4.wireOp",EDGE,"E41.2.3")}),1.0]])]});
            var Q7;
            Q7=makeQuery(id+"F4.imprint","IMPRINT",FACE,{"disambiguationData":[TD([[makeQuery(id+"F4.imprint","IMPRINT",EDGE,{"derivedFrom":sQuery(id+"F4.wireOp",EDGE,"E41.3.3")}),1.0]])]});
            var Q8;
            Q8=makeQuery(id+"F4.imprint","IMPRINT",FACE,{"disambiguationData":[TD([[makeQuery(id+"F4.imprint","IMPRINT",EDGE,{"derivedFrom":sQuery(id+"F4.wireOp",EDGE,"E41.4.3")}),1.0]])]});
            extrude(context, id + "F5", {"entities" : qUnion([Q0, Q1, Q2, Q3, Q4, Q5, Q6, Q7, Q8]), "operationType" : NewBodyOperationType.ADD, "depth" : 0.03 * mm});
        }
        {
            var Q0;
            Q0=qCreatedBy(makeId("Right.planeOp"),FACE);
            var sketch = newSketch(context, id + "F6", { "sketchPlane" : qUnion([Q0])});
            skArc(sketch, "E43", {"start": v(-25.4, 431.8) * mm, "mid": v(-97.24, 402.04) * mm, "end": v(-127, 330.2) * mm});
            skArc(sketch, "E44.0", {"start": v(-25.4, 428.63) * mm, "mid": v(-95, 399.8) * mm, "end": v(-123.83, 330.2) * mm});
            skLineSegment(sketch, "E45", {"start": v(-25.4, 428.63) * mm, "end": v(-25.4, 431.8) * mm});
            skLineSegment(sketch, "E46", {"start": v(-127, 330.2) * mm, "end": v(-123.83, 330.2) * mm});
            skSolve(sketch);
        }
        {
            var Q0;
            Q0=makeQuery(id+"F6.imprint","IMPRINT",FACE,{"disambiguationData":[TD([[makeQuery(id+"F6.imprint","IMPRINT",EDGE,{"derivedFrom":sQuery(id+"F6.wireOp",EDGE,"E43")}),1.0]])]});
            var Q1;
            Q1=sQuery(id+"F6.wireOp",EDGE,"E46");
            revolve(context, id + "F7", {"entities" : qUnion([Q0]), "axis" : qUnion([Q1]), "revolveType" : RevolveType.FULL});
        }
        {
            var Q0;
            Q0=makeQuery(id+"F5.opExtrude","SWEPT_BODY",BODY,{"disambiguationData":[OSD([sQuery(id+"F4.wireOp",EDGE,"E42.4.1"),sQuery(id+"F4.wireOp",EDGE,"E42.4.2"),sQuery(id+"F4.wireOp",EDGE,"E42.4.3"),sQuery(id+"F4.wireOp",EDGE,"E42.4.6"),sQuery(id+"F4.wireOp",EDGE,"E42.4.7"),sQuery(id+"F4.wireOp",EDGE,"E42.4.8"),sQuery(id+"F4.wireOp",EDGE,"E42.4.9"),sQuery(id+"F4.wireOp",EDGE,"E42.4.10")])]});
            var Q1;
            Q1=makeQuery(id+"F5.opExtrude","SWEPT_BODY",BODY,{"disambiguationData":[OSD([sQuery(id+"F4.wireOp",EDGE,"E42.3.1"),sQuery(id+"F4.wireOp",EDGE,"E42.3.2"),sQuery(id+"F4.wireOp",EDGE,"E42.3.3"),sQuery(id+"F4.wireOp",EDGE,"E42.3.6"),sQuery(id+"F4.wireOp",EDGE,"E42.3.7"),sQuery(id+"F4.wireOp",EDGE,"E42.3.8"),sQuery(id+"F4.wireOp",EDGE,"E42.3.9"),sQuery(id+"F4.wireOp",EDGE,"E42.3.10")])]});
            var Q2;
            Q2=makeQuery(id+"F5.opExtrude","SWEPT_BODY",BODY,{"disambiguationData":[OSD([sQuery(id+"F4.wireOp",EDGE,"E42.2.1"),sQuery(id+"F4.wireOp",EDGE,"E42.2.2"),sQuery(id+"F4.wireOp",EDGE,"E42.2.3"),sQuery(id+"F4.wireOp",EDGE,"E42.2.6"),sQuery(id+"F4.wireOp",EDGE,"E42.2.7"),sQuery(id+"F4.wireOp",EDGE,"E42.2.8"),sQuery(id+"F4.wireOp",EDGE,"E42.2.9"),sQuery(id+"F4.wireOp",EDGE,"E42.2.10")])]});
            var Q3;
            Q3=makeQuery(id+"F5.opExtrude","SWEPT_BODY",BODY,{"disambiguationData":[OSD([sQuery(id+"F4.wireOp",EDGE,"E42.1.1"),sQuery(id+"F4.wireOp",EDGE,"E42.1.2"),sQuery(id+"F4.wireOp",EDGE,"E42.1.3"),sQuery(id+"F4.wireOp",EDGE,"E42.1.6"),sQuery(id+"F4.wireOp",EDGE,"E42.1.7"),sQuery(id+"F4.wireOp",EDGE,"E42.1.8"),sQuery(id+"F4.wireOp",EDGE,"E42.1.9"),sQuery(id+"F4.wireOp",EDGE,"E42.1.10")])]});
            var Q4;
            Q4=makeQuery(id+"F5.opExtrude","SWEPT_BODY",BODY,{"disambiguationData":[OSD([sQuery(id+"F4.wireOp",EDGE,"E41.4.3"),sQuery(id+"F4.wireOp",EDGE,"E41.4.4"),sQuery(id+"F4.wireOp",EDGE,"E41.4.5"),sQuery(id+"F4.wireOp",EDGE,"E41.4.6"),sQuery(id+"F4.wireOp",EDGE,"E41.4.7"),sQuery(id+"F4.wireOp",EDGE,"E41.4.8"),sQuery(id+"F4.wireOp",EDGE,"E41.4.9"),sQuery(id+"F4.wireOp",EDGE,"E41.4.10")])]});
            var Q5;
            Q5=makeQuery(id+"F5.opExtrude","SWEPT_BODY",BODY,{"disambiguationData":[OSD([sQuery(id+"F4.wireOp",EDGE,"E41.3.3"),sQuery(id+"F4.wireOp",EDGE,"E41.3.4"),sQuery(id+"F4.wireOp",EDGE,"E41.3.5"),sQuery(id+"F4.wireOp",EDGE,"E41.3.6"),sQuery(id+"F4.wireOp",EDGE,"E41.3.7"),sQuery(id+"F4.wireOp",EDGE,"E41.3.8"),sQuery(id+"F4.wireOp",EDGE,"E41.3.9"),sQuery(id+"F4.wireOp",EDGE,"E41.3.10")])]});
            var Q6;
            Q6=makeQuery(id+"F5.opExtrude","SWEPT_BODY",BODY,{"disambiguationData":[OSD([sQuery(id+"F4.wireOp",EDGE,"E41.2.3"),sQuery(id+"F4.wireOp",EDGE,"E41.2.4"),sQuery(id+"F4.wireOp",EDGE,"E41.2.5"),sQuery(id+"F4.wireOp",EDGE,"E41.2.6"),sQuery(id+"F4.wireOp",EDGE,"E41.2.7"),sQuery(id+"F4.wireOp",EDGE,"E41.2.8"),sQuery(id+"F4.wireOp",EDGE,"E41.2.9"),sQuery(id+"F4.wireOp",EDGE,"E41.2.10")])]});
            var Q7;
            Q7=makeQuery(id+"F5.opExtrude","SWEPT_BODY",BODY,{"disambiguationData":[OSD([sQuery(id+"F4.wireOp",EDGE,"E33"),sQuery(id+"F4.wireOp",EDGE,"E34"),sQuery(id+"F4.wireOp",EDGE,"E35"),sQuery(id+"F4.wireOp",EDGE,"E36"),sQuery(id+"F4.wireOp",EDGE,"E37.filletArc"),sQuery(id+"F4.wireOp",EDGE,"E38.filletArc"),sQuery(id+"F4.wireOp",EDGE,"E39.filletArc"),sQuery(id+"F4.wireOp",EDGE,"E40.filletArc")])]});
            var Q8;
            Q8=makeQuery(id+"F3.opExtrude","SWEPT_BODY",BODY,{"disambiguationData":[OSD([sQuery(id+"F2.wireOp",EDGE,"E17"),sQuery(id+"F2.wireOp",EDGE,"E18"),sQuery(id+"F2.wireOp",EDGE,"E19"),sQuery(id+"F2.wireOp",EDGE,"E20.filletArc"),sQuery(id+"F2.wireOp",EDGE,"E21.filletArc"),sQuery(id+"F2.wireOp",EDGE,"E22"),sQuery(id+"F2.wireOp",EDGE,"E24.0"),sQuery(id+"F2.wireOp",EDGE,"E25.0"),sQuery(id+"F2.wireOp",EDGE,"E26.0"),sQuery(id+"F2.wireOp",EDGE,"E27.0"),sQuery(id+"F2.wireOp",EDGE,"E28.filletArc"),sQuery(id+"F2.wireOp",EDGE,"E29.filletArc")])]});
            var Q9;
            Q9=makeQuery(id+"F5.opExtrude","SWEPT_BODY",BODY,{"disambiguationData":[OSD([sQuery(id+"F4.wireOp",EDGE,"E41.1.3"),sQuery(id+"F4.wireOp",EDGE,"E41.1.4"),sQuery(id+"F4.wireOp",EDGE,"E41.1.5"),sQuery(id+"F4.wireOp",EDGE,"E41.1.6"),sQuery(id+"F4.wireOp",EDGE,"E41.1.7"),sQuery(id+"F4.wireOp",EDGE,"E41.1.8"),sQuery(id+"F4.wireOp",EDGE,"E41.1.9"),sQuery(id+"F4.wireOp",EDGE,"E41.1.10")])]});
            var Q10;
            Q10=makeQuery(id+"F1.opExtrude","CAP_EDGE",EDGE,{"disambiguationData":[OSD([sQuery(id+"F0.wireOp",EDGE,"E2")])],"isStart":true});
            circularPattern(context, id + "F8", {"entities" : qUnion([Q0, Q1, Q2, Q3, Q4, Q5, Q6, Q7, Q8, Q9]), "axis" : qUnion([Q10]), "angle" : 360 * degree, "instanceCount" : 6, "equalSpace" : true});
        }
        {
            var Q0;
            Q0=qCreatedBy(makeId("Top.planeOp"),FACE);
            var sketch = newSketch(context, id + "F9", { "sketchPlane" : qUnion([Q0])});
            skLineSegment(sketch, "E47", {"start": v(0, 80) * mm, "end": v(5, 80) * mm});
            skLineSegment(sketch, "E48", {"start": v(5, 80) * mm, "end": v(5, 60) * mm});
            skLineSegment(sketch, "E49", {"start": v(5, 60) * mm, "end": v(10, 60) * mm});
            skLineSegment(sketch, "E50", {"start": v(10, 60) * mm, "end": v(10, -60) * mm});
            skLineSegment(sketch, "E51", {"start": v(10, -60) * mm, "end": v(5, -60) * mm});
            skLineSegment(sketch, "E52", {"start": v(5, -60) * mm, "end": v(5, -80) * mm});
            skLineSegment(sketch, "E53", {"start": v(5, -80) * mm, "end": v(0, -80) * mm});
            skLineSegment(sketch, "E54", {"start": v(0, -80) * mm, "end": v(0, 80) * mm});
            skLineSegment(sketch, "E55", {"start": v(11, 55) * mm, "end": v(17.46, 55) * mm});
            skLineSegment(sketch, "E56", {"start": v(17.46, 55) * mm, "end": v(17.46, 47.5) * mm});
            skLineSegment(sketch, "E57", {"start": v(17.46, 47.5) * mm, "end": v(19.46, 47.5) * mm});
            skLineSegment(sketch, "E58", {"start": v(19.46, 47.5) * mm, "end": v(19.46, 45) * mm});
            skLineSegment(sketch, "E59", {"start": v(19.46, 45) * mm, "end": v(26.5, 45) * mm});
            skLineSegment(sketch, "E60", {"start": v(26.5, 45) * mm, "end": v(26.5, 42) * mm});
            skLineSegment(sketch, "E61", {"start": v(26.5, 42) * mm, "end": v(19.46, 42) * mm});
            skLineSegment(sketch, "E62", {"start": v(19.46, 42) * mm, "end": v(19.46, -42) * mm});
            skLineSegment(sketch, "E63", {"start": v(19.46, -42) * mm, "end": v(26.5, -42) * mm});
            skLineSegment(sketch, "E64", {"start": v(26.5, -42) * mm, "end": v(26.5, -45) * mm});
            skLineSegment(sketch, "E65", {"start": v(26.5, -45) * mm, "end": v(19.46, -45) * mm});
            skLineSegment(sketch, "E66", {"start": v(19.46, -45) * mm, "end": v(19.46, -47.5) * mm});
            skLineSegment(sketch, "E67", {"start": v(19.46, -47.5) * mm, "end": v(17.46, -47.5) * mm});
            skLineSegment(sketch, "E68", {"start": v(17.46, -47.5) * mm, "end": v(17.46, -55) * mm});
            skLineSegment(sketch, "E69", {"start": v(17.46, -55) * mm, "end": v(11, -55) * mm});
            skLineSegment(sketch, "E70", {"start": v(11, -55) * mm, "end": v(11, 55) * mm});
            skPoint(sketch, "E71", {"position": v(11, 0) * mm});
            skSolve(sketch);
        }
        {
            var Q0;
            Q0=makeQuery(id+"F9.imprint","IMPRINT",FACE,{"disambiguationData":[TD([[makeQuery(id+"F9.imprint","IMPRINT",EDGE,{"derivedFrom":sQuery(id+"F9.wireOp",EDGE,"E47")}),-1.0]])]});
            var Q1;
            Q1=makeQuery(id+"F9.imprint","IMPRINT",FACE,{"disambiguationData":[TD([[makeQuery(id+"F9.imprint","IMPRINT",EDGE,{"derivedFrom":sQuery(id+"F9.wireOp",EDGE,"E55")}),-1.0]])]});
            var Q2;
            Q2=sQuery(id+"F9.wireOp",EDGE,"E54");
            revolve(context, id + "F10", {"entities" : qUnion([Q0, Q1]), "axis" : qUnion([Q2]), "revolveType" : RevolveType.FULL});
        }
        {
            var Q0;
            Q0=makeQuery(id+"F10.opRevolve","SWEPT_FACE",FACE,{"disambiguationData":[OSD([sQuery(id+"F9.wireOp",EDGE,"E51")])]});
            cPlane(context, id + "F11", {"entities" : qUnion([Q0]), "cplaneType" : CPlaneType.OFFSET, "offset" : 6.35 * mm, "width" : 152.4 * mm, "height" : 152.4 * mm});
        }
        {
            var Q0;
            Q0=qCreatedBy(id+"F11.planeOp",FACE);
            var sketch = newSketch(context, id + "F12", { "sketchPlane" : qUnion([Q0])});
            skArc(sketch, "E72", {"start": v(-5.25, 0) * mm, "mid": v(0, -5.25) * mm, "end": v(5.25, 0) * mm});
            skLineSegment(sketch, "E73", {"start": v(5.25, 0) * mm, "end": v(5.25, 12.7) * mm});
            skLineSegment(sketch, "E74", {"start": v(5.25, 12.7) * mm, "end": v(24.3, 12.7) * mm});
            skLineSegment(sketch, "E75", {"start": v(24.3, 12.7) * mm, "end": v(114.3, -419.1) * mm});
            skLineSegment(sketch, "E76", {"start": v(114.3, -419.1) * mm, "end": v(-114.3, -419.1) * mm});
            skLineSegment(sketch, "E77", {"start": v(-114.3, -419.1) * mm, "end": v(-24.3, 12.7) * mm});
            skLineSegment(sketch, "E78", {"start": v(-24.3, 12.7) * mm, "end": v(-5.25, 12.7) * mm});
            skLineSegment(sketch, "E79", {"start": v(-5.25, 12.7) * mm, "end": v(-5.25, 0) * mm});
            skLineSegment(sketch, "E80", {"start": v(0, 0) * mm, "end": v(0, -419.1) * mm, "construction": true});
            skPoint(sketch, "E80.endSnap0", {"position": v(0, -5.25) * mm});
            skLineSegment(sketch, "E81", {"start": v(27.54, 12.7) * mm, "end": v(117.54, -419.1) * mm});
            skLineSegment(sketch, "E82", {"start": v(24.3, 12.7) * mm, "end": v(27.54, 12.7) * mm});
            skLineSegment(sketch, "E83", {"start": v(114.3, -419.1) * mm, "end": v(117.54, -419.1) * mm});
            skLineSegment(sketch, "E84", {"start": v(-24.3, 12.7) * mm, "end": v(-27.54, 12.7) * mm});
            skLineSegment(sketch, "E85", {"start": v(-27.54, 12.7) * mm, "end": v(-117.54, -419.1) * mm});
            skLineSegment(sketch, "E86", {"start": v(-117.54, -419.1) * mm, "end": v(-114.3, -419.1) * mm});
            skSolve(sketch);
        }
        {
            var Q0;
            {var subQ0=sQuery(id+"F12.wireOp",EDGE,"E74");Q0=makeQuery(id+"F12.imprint","IMPRINT",FACE,{"disambiguationData":[TD([[makeQuery(id+"F12.imprint","IMPRINT",EDGE,{"derivedFrom":subQ0}),-1.0]])]});}
            var Q1;
            {var subQ0=sQuery(id+"F12.wireOp",EDGE,"E72");Q1=makeQuery(id+"F12.imprint","IMPRINT",FACE,{"disambiguationData":[TD([[makeQuery(id+"F12.imprint","IMPRINT",EDGE,{"derivedFrom":subQ0}),-1.0]])]});}
            extrude(context, id + "F13", {"entities" : qUnion([Q0, Q1]), "oppositeDirection" : true, "depth" : 6.35 * mm});
        }
        {
            var Q0;
            Q0=makeQuery(id+"F12.imprint","IMPRINT",FACE,{"disambiguationData":[TD([[makeQuery(id+"F12.imprint","IMPRINT",EDGE,{"derivedFrom":sQuery(id+"F12.wireOp",EDGE,"E75")}),1.0]])]});
            var Q1;
            Q1=makeQuery(id+"F12.imprint","IMPRINT",FACE,{"disambiguationData":[TD([[makeQuery(id+"F12.imprint","IMPRINT",EDGE,{"derivedFrom":sQuery(id+"F12.wireOp",EDGE,"E77")}),1.0]])]});
            extrude(context, id + "F14", {"entities" : qUnion([Q0, Q1]), "oppositeDirection" : true, "depth" : 6.35 * mm});
        }
        {
            var Q0;
            Q0=makeQuery(id+"F12.imprint","IMPRINT",FACE,{"disambiguationData":[TD([[makeQuery(id+"F12.imprint","IMPRINT",EDGE,{"derivedFrom":sQuery(id+"F12.wireOp",EDGE,"E75")}),1.0]])]});
            var Q1;
            Q1=sQuery(id+"F12.wireOp",EDGE,"E80");
            revolve(context, id + "F15", {"operationType" : NewBodyOperationType.ADD, "entities" : qUnion([Q0]), "axis" : qUnion([Q1]), "revolveType" : RevolveType.ONE_DIRECTION, "angle" : 180 * degree});
        }
        {
            var Q0;
            {var subQ0=sQuery(id+"F12.wireOp",EDGE,"E83");Q0=makeQuery(id+"F20.boolean.opBoolean","MERGE",FACE,{"derivedFrom":[makeQuery(id+"F13.opExtrude","SWEPT_FACE",FACE,{"disambiguationData":[OSD([sQuery(id+"F12.wireOp",EDGE,"E76")])]}),makeQuery(id+"F15.boolean.opBoolean","MERGE",FACE,{"derivedFrom":[makeQuery(id+"F14.opExtrude","SWEPT_FACE",FACE,{"disambiguationData":[OSD([subQ0])]}),makeQuery(id+"F14.opExtrude","SWEPT_FACE",FACE,{"disambiguationData":[OSD([sQuery(id+"F12.wireOp",EDGE,"E86")])]}),makeQuery(id+"F15.opRevolve","SWEPT_FACE",FACE,{"disambiguationData":[OSD([subQ0])]})]})]});}
            var sketch = newSketch(context, id + "F16", { "sketchPlane" : qUnion([Q0])});
            skArc(sketch, "E87", {"start": v(0, 209.3) * mm, "mid": v(61.28, 195.49) * mm, "end": v(110.73, 156.74) * mm});
            skPoint(sketch, "E88", {"position": v(117.54, 60) * mm});
            skCircle(sketch, "E89", {"center": v(0, 196.6) * mm, "radius": 4.76 * mm});
            skCircle(sketch, "E90.1.0", {"center": v(92.1, 158.45) * mm, "radius": 4.76 * mm});
            skLineSegment(sketch, "E90.anchor1", {"start": v(0, 34.6) * mm, "end": v(0, 209.3) * mm, "construction": true});
            skLineSegment(sketch, "E90.anchor2", {"start": v(0, 66.35) * mm, "end": v(92.1, 158.45) * mm, "construction": true});
            skCircle(sketch, "E91", {"center": v(181.04, 47.3) * mm, "radius": 4.76 * mm});
            skCircle(sketch, "E92", {"center": v(90.52, 47.3) * mm, "radius": 4.76 * mm});
            skLineSegment(sketch, "E93", {"start": v(90.52, 47.3) * mm, "end": v(181.04, 47.3) * mm, "construction": true});
            skLineSegment(sketch, "E94", {"start": v(90.52, 47.3) * mm, "end": v(0, 47.3) * mm, "construction": true});
            skCircle(sketch, "E95.MirrorC", {"center": v(-181.04, 47.3) * mm, "radius": 4.76 * mm});
            skCircle(sketch, "E96", {"center": v(142.94, 101.28) * mm, "radius": 19.05 * mm});
            skArc(sketch, "E97.0", {"start": v(193.74, 101.28) * mm, "mid": v(178.86, 137.2) * mm, "end": v(142.94, 152.08) * mm});
            skLineSegment(sketch, "E98", {"start": v(142.94, 152.08) * mm, "end": v(120.57, 152.08) * mm});
            skLineSegment(sketch, "E99", {"start": v(193.74, 101.28) * mm, "end": v(193.74, 40.95) * mm});
            skPoint(sketch, "E100.visualSharp", {"position": v(193.74, 34.6) * mm});
            skArc(sketch, "E100.filletArc", {"start": v(187.4, 34.6) * mm, "mid": v(191.88, 36.46) * mm, "end": v(193.74, 40.95) * mm});
            skArc(sketch, "E101.filletArc", {"start": v(110.73, 156.74) * mm, "mid": v(115.13, 153.3) * mm, "end": v(120.57, 152.08) * mm});
            skCircle(sketch, "E102.0", {"center": v(142.94, 101.28) * mm, "radius": 15.88 * mm});
            skCircle(sketch, "E103", {"center": v(0, 47.3) * mm, "radius": 4.76 * mm});
            skCircle(sketch, "E104", {"center": v(169.88, 128.22) * mm, "radius": 4.76 * mm});
            skLineSegment(sketch, "E105", {"start": v(142.94, 101.28) * mm, "end": v(169.88, 128.22) * mm, "construction": true});
            skCircle(sketch, "E106.0", {"center": v(142.94, 101.28) * mm, "radius": 22.23 * mm});
            skLineSegment(sketch, "E107", {"start": v(0, 34.6) * mm, "end": v(187.4, 34.6) * mm});
            skArc(sketch, "E108.0.0", {"start": v(27.54, 66.35) * mm, "mid": v(0, 93.9) * mm, "end": v(-27.54, 66.35) * mm});
            skLineSegment(sketch, "E108.0.1", {"start": v(-27.54, 66.35) * mm, "end": v(-117.54, 66.35) * mm});
            skArc(sketch, "E108.0.2", {"start": v(-117.54, 66.35) * mm, "mid": v(0, 183.9) * mm, "end": v(117.54, 66.35) * mm});
            skLineSegment(sketch, "E108.0.3", {"start": v(117.54, 66.35) * mm, "end": v(27.54, 66.35) * mm});
            skCircle(sketch, "E109.MirrorC", {"center": v(-169.88, 128.22) * mm, "radius": 4.76 * mm});
            skCircle(sketch, "E110.MirrorC", {"center": v(-90.52, 47.3) * mm, "radius": 4.76 * mm});
            skLineSegment(sketch, "E111.MirrorCS", {"start": v(0, 34.6) * mm, "end": v(-187.4, 34.6) * mm});
            skArc(sketch, "E112.MirrorCS", {"start": v(-187.4, 34.6) * mm, "mid": v(-191.88, 36.46) * mm, "end": v(-193.74, 40.95) * mm});
            skLineSegment(sketch, "E113.MirrorCS", {"start": v(-142.94, 152.08) * mm, "end": v(-120.57, 152.08) * mm});
            skLineSegment(sketch, "E114.MirrorCS", {"start": v(-193.74, 101.28) * mm, "end": v(-193.74, 40.95) * mm});
            skArc(sketch, "E115.MirrorCS", {"start": v(-193.74, 101.28) * mm, "mid": v(-178.86, 137.2) * mm, "end": v(-142.94, 152.08) * mm});
            skArc(sketch, "E116.MirrorCS", {"start": v(-110.73, 156.74) * mm, "mid": v(-115.13, 153.3) * mm, "end": v(-120.57, 152.08) * mm});
            skCircle(sketch, "E117.MirrorC", {"center": v(-92.1, 158.45) * mm, "radius": 4.76 * mm});
            skArc(sketch, "E118.MirrorCS", {"start": v(0, 209.3) * mm, "mid": v(-61.28, 195.49) * mm, "end": v(-110.73, 156.74) * mm});
            skCircle(sketch, "E119.MirrorC", {"center": v(-142.94, 101.28) * mm, "radius": 22.23 * mm});
            skCircle(sketch, "E120.MirrorC", {"center": v(-142.94, 101.28) * mm, "radius": 19.05 * mm});
            skCircle(sketch, "E121.MirrorC", {"center": v(-142.94, 101.28) * mm, "radius": 15.88 * mm});
            skSolve(sketch);
        }
        {
            var Q0;
            {var subQ0=sQuery(id+"F12.wireOp",EDGE,"E76");Q0=makeQuery(id+"F16.imprint","IMPRINT",FACE,{"disambiguationData":[TD([[makeQuery(id+"F16.imprint","IMPRINT",EDGE,{"derivedFrom":makeQuery(id+"F13.opExtrude","CAP_EDGE",EDGE,{"disambiguationData":[OSD([subQ0])],"isStart":true})}),-1.0]])]});}
            var Q1;
            {var subQ1=sQuery(id+"F12.wireOp",EDGE,"E76");Q1=makeQuery(id+"F16.imprint","IMPRINT",FACE,{"disambiguationData":[TD([[makeQuery(id+"F16.imprint","IMPRINT",EDGE,{"derivedFrom":makeQuery(id+"F13.opExtrude","CAP_EDGE",EDGE,{"disambiguationData":[OSD([subQ1])],"isStart":true})}),1.0]])]});}
            var Q2;
            {var subQ0=sQuery(id+"F12.wireOp",EDGE,"E83");Q2=makeQuery(id+"F16.imprint","IMPRINT",FACE,{"disambiguationData":[TD([[makeQuery(id+"F16.imprint","IMPRINT",EDGE,{"derivedFrom":makeQuery(id+"F14.opExtrude","CAP_EDGE",EDGE,{"disambiguationData":[OSD([subQ0])],"isStart":false})}),1.0]])]});}
            var Q3;
            {var subQ0=sQuery(id+"F16.wireOp",EDGE,"E108.0.0");Q3=makeQuery(id+"F16.imprint","IMPRINT",FACE,{"disambiguationData":[TD([[makeQuery(id+"F16.imprint","IMPRINT",EDGE,{"derivedFrom":subQ0}),-1.0]])]});}
            var Q4;
            {var subQ2=sQuery(id+"F12.wireOp",EDGE,"E86");Q4=makeQuery(id+"F16.imprint","IMPRINT",FACE,{"disambiguationData":[TD([[makeQuery(id+"F16.imprint","IMPRINT",EDGE,{"derivedFrom":makeQuery(id+"F14.opExtrude","CAP_EDGE",EDGE,{"disambiguationData":[OSD([subQ2])],"isStart":false})}),1.0]])]});}
            var Q5;
            {var subQ6=sQuery(id+"F16.wireOp",EDGE,"E108.0.2");Q5=makeQuery(id+"F16.imprint","IMPRINT",FACE,{"disambiguationData":[TD([[makeQuery(id+"F16.imprint","IMPRINT",EDGE,{"derivedFrom":subQ6}),-1.0]])]});}
            var Q6;
            Q6=makeQuery(id+"F16.imprint","IMPRINT",FACE,{"disambiguationData":[TD([[makeQuery(id+"F16.imprint","IMPRINT",EDGE,{"derivedFrom":sQuery(id+"F16.wireOp",EDGE,"E87")}),-1.0]])]});
            var Q7;
            Q7=makeQuery(id+"F16.imprint","IMPRINT",FACE,{"disambiguationData":[TD([[makeQuery(id+"F16.imprint","IMPRINT",EDGE,{"derivedFrom":sQuery(id+"F16.wireOp",EDGE,"E121.MirrorC")}),-1.0]])]});
            var Q8;
            Q8=makeQuery(id+"F16.imprint","IMPRINT",FACE,{"disambiguationData":[TD([[makeQuery(id+"F16.imprint","IMPRINT",EDGE,{"derivedFrom":sQuery(id+"F16.wireOp",EDGE,"E120.MirrorC")}),-1.0]])]});
            var Q9;
            Q9=makeQuery(id+"F16.imprint","IMPRINT",FACE,{"disambiguationData":[TD([[makeQuery(id+"F16.imprint","IMPRINT",EDGE,{"derivedFrom":sQuery(id+"F16.wireOp",EDGE,"E119.MirrorC")}),-1.0]])]});
            var Q10;
            Q10=makeQuery(id+"F16.imprint","IMPRINT",FACE,{"disambiguationData":[TD([[makeQuery(id+"F16.imprint","IMPRINT",EDGE,{"derivedFrom":sQuery(id+"F16.wireOp",EDGE,"E102.0")}),1.0]])]});
            var Q11;
            Q11=makeQuery(id+"F16.imprint","IMPRINT",FACE,{"disambiguationData":[TD([[makeQuery(id+"F16.imprint","IMPRINT",EDGE,{"derivedFrom":sQuery(id+"F16.wireOp",EDGE,"E96")}),1.0]])]});
            var Q12;
            Q12=makeQuery(id+"F16.imprint","IMPRINT",FACE,{"disambiguationData":[TD([[makeQuery(id+"F16.imprint","IMPRINT",EDGE,{"derivedFrom":sQuery(id+"F16.wireOp",EDGE,"E96")}),-1.0]])]});
            extrude(context, id + "F17", {"entities" : qUnion([Q0, Q1, Q2, Q3, Q4, Q5, Q6, Q7, Q8, Q9, Q10, Q11, Q12]), "depth" : 6.35 * mm});
        }
        {
            var Q0;
            Q0=makeQuery(id+"F16.imprint","IMPRINT",FACE,{"disambiguationData":[TD([[makeQuery(id+"F16.imprint","IMPRINT",EDGE,{"derivedFrom":sQuery(id+"F16.wireOp",EDGE,"E96")}),-1.0]])]});
            var Q1;
            Q1=makeQuery(id+"F16.imprint","IMPRINT",FACE,{"disambiguationData":[TD([[makeQuery(id+"F16.imprint","IMPRINT",EDGE,{"derivedFrom":sQuery(id+"F16.wireOp",EDGE,"E119.MirrorC")}),-1.0]])]});
            extrude(context, id + "F18", {"entities" : qUnion([Q0, Q1]), "operationType" : NewBodyOperationType.ADD, "oppositeDirection" : true, "depth" : 76.2 * mm});
        }
        {
            var Q0;
            Q0=makeQuery(id+"F16.imprint","IMPRINT",FACE,{"disambiguationData":[TD([[makeQuery(id+"F16.imprint","IMPRINT",EDGE,{"derivedFrom":sQuery(id+"F16.wireOp",EDGE,"E120.MirrorC")}),-1.0]])]});
            var Q1;
            Q1=makeQuery(id+"F16.imprint","IMPRINT",FACE,{"disambiguationData":[TD([[makeQuery(id+"F16.imprint","IMPRINT",EDGE,{"derivedFrom":sQuery(id+"F16.wireOp",EDGE,"E96")}),1.0]])]});
            extrude(context, id + "F19", {"entities" : qUnion([Q0, Q1]), "operationType" : NewBodyOperationType.ADD, "oppositeDirection" : true, "depth" : 908.05 * mm});
        }
        {
            var Q0;
            Q0=makeQuery(id+"F14.opExtrude","SWEPT_BODY",BODY,{"disambiguationData":[OSD([sQuery(id+"F12.wireOp",EDGE,"E75"),sQuery(id+"F12.wireOp",EDGE,"E81"),sQuery(id+"F12.wireOp",EDGE,"E82"),sQuery(id+"F12.wireOp",EDGE,"E83")])]});
            var Q1;
            Q1=makeQuery(id+"F13.opExtrude","SWEPT_BODY",BODY,{"disambiguationData":[OSD([sQuery(id+"F12.wireOp",EDGE,"E72"),sQuery(id+"F12.wireOp",EDGE,"E73"),sQuery(id+"F12.wireOp",EDGE,"E74"),sQuery(id+"F12.wireOp",EDGE,"E75"),sQuery(id+"F12.wireOp",EDGE,"E76"),sQuery(id+"F12.wireOp",EDGE,"E77"),sQuery(id+"F12.wireOp",EDGE,"E78"),sQuery(id+"F12.wireOp",EDGE,"E79")])]});
            var Q2;
            Q2=makeQuery(id+"F7.opRevolve","SWEPT_BODY",BODY,{"disambiguationData":[OSD([sQuery(id+"F6.wireOp",EDGE,"E43"),sQuery(id+"F6.wireOp",EDGE,"E44.0"),sQuery(id+"F6.wireOp",EDGE,"E45"),sQuery(id+"F6.wireOp",EDGE,"E46")])]});
            var Q3;
            Q3=makeQuery(id+"F17.opExtrude","SWEPT_BODY",BODY,{"disambiguationData":[OSD([sQuery(id+"F12.wireOp",EDGE,"E75"),sQuery(id+"F12.wireOp",EDGE,"E76"),sQuery(id+"F12.wireOp",EDGE,"E77"),sQuery(id+"F12.wireOp",EDGE,"E81"),sQuery(id+"F12.wireOp",EDGE,"E83"),sQuery(id+"F12.wireOp",EDGE,"E85"),sQuery(id+"F12.wireOp",EDGE,"E86"),sQuery(id+"F16.wireOp",EDGE,"E87"),sQuery(id+"F16.wireOp",EDGE,"VFqkfk9x-Qrqq-CKIK-GWJ0-ICVU9IZnEM31"),sQuery(id+"F16.wireOp",EDGE,"vjkyok6X-AUT5-f6Be-fc00-L9xAfVbjv4x5"),sQuery(id+"F16.wireOp",EDGE,"y1T3sMc3-Syo6-1Iq8-z5ZJ-pRIH1ES55dxk"),sQuery(id+"F16.wireOp",EDGE,"e2ccab49-0059-43cb-a543-7f5852d39230.filletArc"),sQuery(id+"F16.wireOp",EDGE,"71700800-8109-41fc-897e-0a9c69a79554.filletArc"),sQuery(id+"F16.wireOp",EDGE,"E90.1.0"),sQuery(id+"F16.wireOp",EDGE,"E91"),sQuery(id+"F16.wireOp",EDGE,"E92"),sQuery(id+"F16.wireOp",EDGE,"f59d4b18-994d-48fc-930b-03e5cf8686390.MirrorC"),sQuery(id+"F16.wireOp",EDGE,"E95.MirrorC"),sQuery(id+"F16.wireOp",EDGE,"f59d4b18-994d-48fc-930b-03e5cf8686392.MirrorC"),sQuery(id+"F16.wireOp",EDGE,"E89")])]});
            var Q4;
            Q4=makeQuery(id+"F19.opExtrude","SWEPT_BODY",BODY,{"disambiguationData":[OSD([sQuery(id+"F16.wireOp",EDGE,"E120.MirrorC"),sQuery(id+"F16.wireOp",EDGE,"E121.MirrorC")])]});
            var Q5;
            Q5=makeQuery(id+"F19.opExtrude","SWEPT_BODY",BODY,{"disambiguationData":[OSD([sQuery(id+"F16.wireOp",EDGE,"E96"),sQuery(id+"F16.wireOp",EDGE,"E102.0")])]});
            var Q6;
            Q6=makeQuery(id+"F18.opExtrude","SWEPT_BODY",BODY,{"disambiguationData":[OSD([sQuery(id+"F16.wireOp",EDGE,"E96"),sQuery(id+"F16.wireOp",EDGE,"E106.0")])]});
            var Q7;
            Q7=makeQuery(id+"F18.opExtrude","SWEPT_BODY",BODY,{"disambiguationData":[OSD([sQuery(id+"F16.wireOp",EDGE,"E119.MirrorC"),sQuery(id+"F16.wireOp",EDGE,"E120.MirrorC")])]});
            var Q8;
            Q8=qCreatedBy(makeId("Front.planeOp"),FACE);
            mirror(context, id + "F20", {"operationType" : NewBodyOperationType.ADD, "entities" : qUnion([Q0, Q1, Q2, Q3, Q4, Q5, Q6, Q7]), "mirrorPlane" : qUnion([Q8])});
        }
    });
